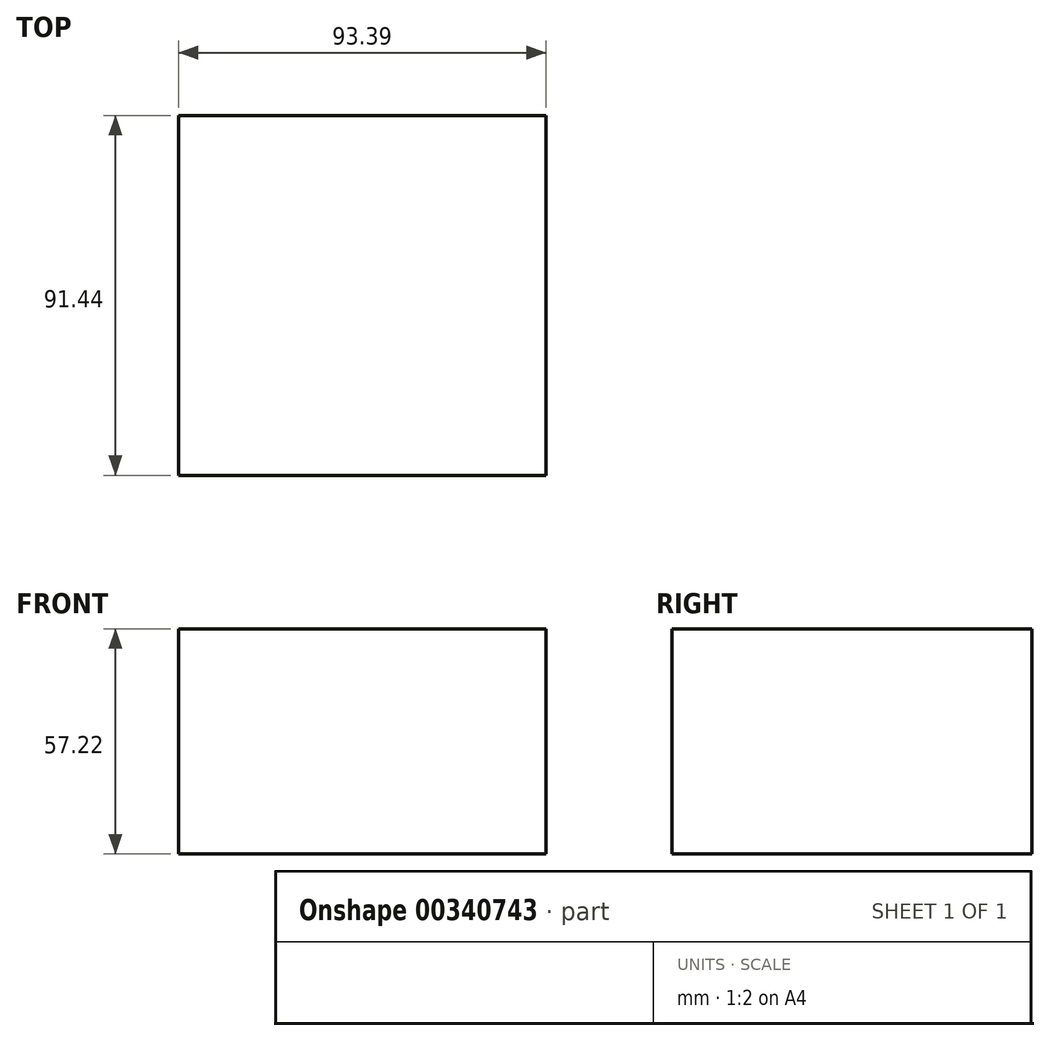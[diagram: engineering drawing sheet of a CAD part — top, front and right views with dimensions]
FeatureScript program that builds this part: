
annotation { "Feature Type Name" : "Feature", "Feature Type Description" : "" }
export const myFeature = defineFeature(function(context is Context, id is Id, definition is map)
    precondition{}
    {
        {
            var Q0;
            Q0=qCreatedBy(makeId("Front.planeOp"),FACE);
            var sketch = newSketch(context, id + "F0", { "sketchPlane" : qUnion([Q0])});
            skLineSegment(sketch, "E0.bottom", {"start": v(0, 0) * mm, "end": v(93.4, 0) * mm});
            skLineSegment(sketch, "E0.top", {"start": v(0, 57.22) * mm, "end": v(93.4, 57.22) * mm});
            skLineSegment(sketch, "E0.left", {"start": v(0, 0) * mm, "end": v(0, 57.22) * mm});
            skLineSegment(sketch, "E0.right", {"start": v(93.4, 0) * mm, "end": v(93.4, 57.22) * mm});
            skSolve(sketch);
        }
        {
            var Q0;
            Q0 = qSketchRegion(id + "F0", true);
            extrude(context, id + "F1", {"entities" : qUnion([Q0]), "depth" : 91.44 * mm});
        }
    });
